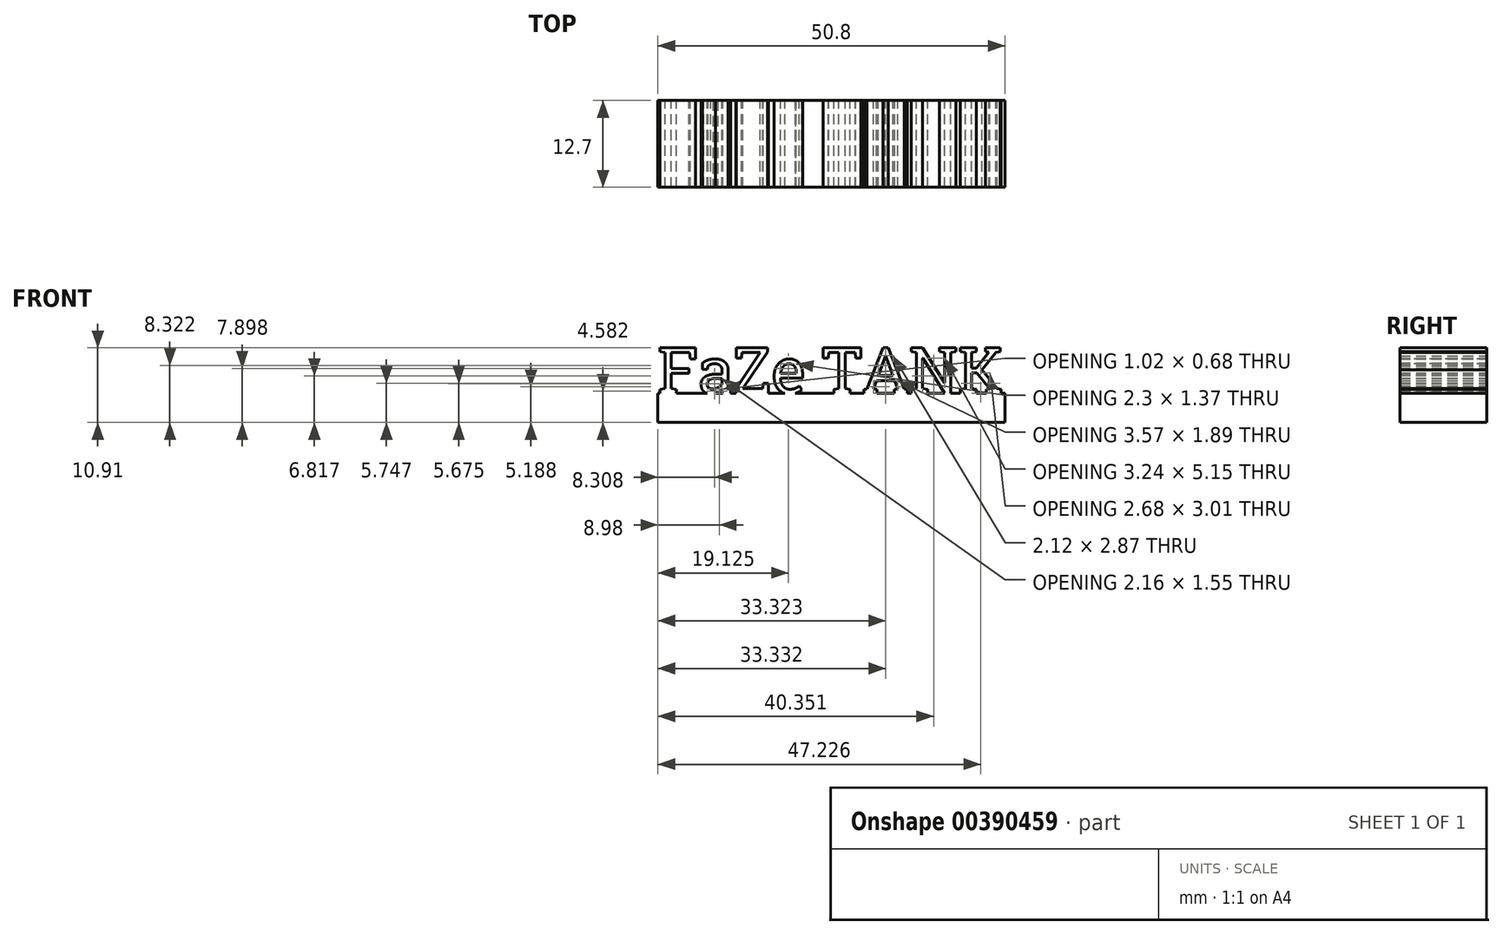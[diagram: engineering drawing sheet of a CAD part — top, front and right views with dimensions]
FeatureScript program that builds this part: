
annotation { "Feature Type Name" : "Feature", "Feature Type Description" : "" }
export const myFeature = defineFeature(function(context is Context, id is Id, definition is map)
    precondition{}
    {
        {
            var Q0;
            Q0=qCreatedBy(makeId("Front.planeOp"),FACE);
            var sketch = newSketch(context, id + "F0", { "sketchPlane" : qUnion([Q0])});
            skText(sketch, "E0", { "text": "FaZe TANK", "fontName": "RobotoSlab-Regular.ttf"});
            skLineSegment(sketch, "E1", {"start": v(-17.1, 4.24) * mm, "end": v(33.7, 4.24) * mm});
            skLineSegment(sketch, "E2", {"start": v(33.7, 0) * mm, "end": v(-17.1, 0) * mm});
            skLineSegment(sketch, "E3", {"start": v(-17.1, 0) * mm, "end": v(-17.1, 4.24) * mm});
            skLineSegment(sketch, "E4", {"start": v(33.7, 4.24) * mm, "end": v(33.7, 0) * mm});
            const initialGuessF0  = {"E0": [-0.0171, 0.00424, 1, 0, 0.00676]};
            skSetInitialGuess(sketch, initialGuessF0);
            skSolve(sketch);
        }
        {
            var Q0;
            Q0 = qSketchRegion(id + "F0", true);
            extrude(context, id + "F1", {"entities" : qUnion([Q0]), "depth" : 12.7 * mm});
        }
    });
